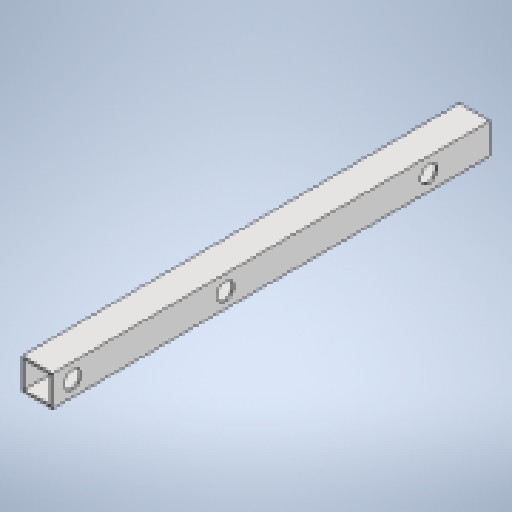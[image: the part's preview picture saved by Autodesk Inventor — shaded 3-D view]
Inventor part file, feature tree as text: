
AUTODESK INVENTOR PART (.ipt)
format: ipt  version: 2025.1 (Build 291241020, 241B)  size: 194,560 bytes
history: native  units: mm
features: extrude x2, sketch x2, projected_geometry x1
ambient origin geometry x8: Origin, YZ Plane, XZ Plane, XY Plane, X Axis, Y Axis, Z Axis, Center Point
bodies: Body1 (feature_tree)
feature tree (5):
  extrude  "Extrusion3"  Depth=30.0mm
  extrude  "Extrusion4"  Depth=2.0mm
  sketch  "Sketch9"  dims[d61=500.0mm d172=30.0mm]
  sketch  "Sketch10"  dims[d173=30.0mm d174=2.0mm d175=420.0mm d176=0.0mm d177=17.0mm d178=17.0mm d179=0.0mm d180=0.0mm d181=30.0mm d182=90.0mm d183=260.0mm d184=435.0mm d185=500.0mm d186=17.0mm]
  projected_geometry  "Projected Loop3"
